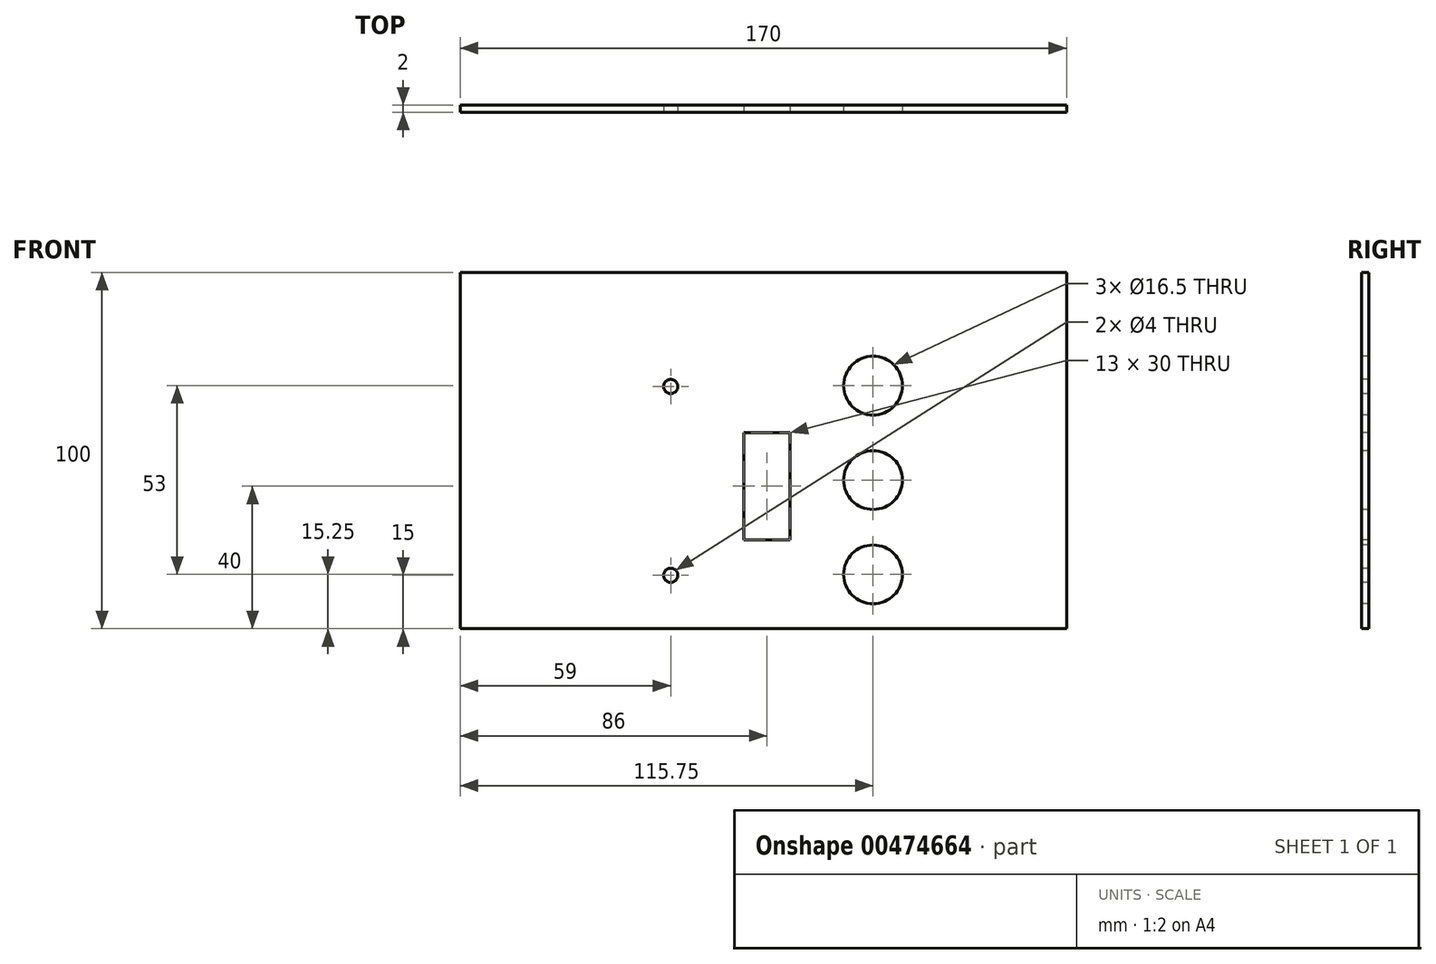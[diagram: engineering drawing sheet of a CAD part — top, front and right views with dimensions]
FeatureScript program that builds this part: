
annotation { "Feature Type Name" : "Feature", "Feature Type Description" : "" }
export const myFeature = defineFeature(function(context is Context, id is Id, definition is map)
    precondition{}
    {
        {
            var Q0;
            Q0=qCreatedBy(makeId("Front.planeOp"),FACE);
            var sketch = newSketch(context, id + "F0", { "sketchPlane" : qUnion([Q0])});
            skLineSegment(sketch, "E0.bottom", {"start": v(85, 50) * mm, "end": v(-85, 50) * mm});
            skLineSegment(sketch, "E0.top", {"start": v(85, -50) * mm, "end": v(-85, -50) * mm});
            skLineSegment(sketch, "E0.left", {"start": v(85, 50) * mm, "end": v(85, -50) * mm});
            skLineSegment(sketch, "E0.right", {"start": v(-85, 50) * mm, "end": v(-85, -50) * mm});
            skPoint(sketch, "E0.middle", {"position": v(0, 0) * mm});
            skSolve(sketch);
        }
        {
            var Q0;
            Q0 = qSketchRegion(id + "F0", true);
            extrude(context, id + "F1", {"entities" : qUnion([Q0]), "depth" : 2 * mm});
        }
        {
            var Q0;
            Q0=makeQuery(id+"F1.opExtrude","CAP_FACE",FACE,{"disambiguationData":[OSD([sQuery(id+"F0.wireOp",EDGE,"E0.bottom"),sQuery(id+"F0.wireOp",EDGE,"E0.top"),sQuery(id+"F0.wireOp",EDGE,"E0.left"),sQuery(id+"F0.wireOp",EDGE,"E0.right")])],"isStart":false});
            var sketch = newSketch(context, id + "F2", { "sketchPlane" : qUnion([Q0])});
            skCircle(sketch, "E1", {"center": v(30.75, -34.75) * mm, "radius": 8.25 * mm});
            skCircle(sketch, "E2", {"center": v(30.75, -8.25) * mm, "radius": 8.25 * mm});
            skCircle(sketch, "E3", {"center": v(30.75, 18.25) * mm, "radius": 8.25 * mm});
            skLineSegment(sketch, "E4.bottom", {"start": v(7.5, -25) * mm, "end": v(-5.5, -25) * mm});
            skLineSegment(sketch, "E4.top", {"start": v(7.5, 5) * mm, "end": v(-5.5, 5) * mm});
            skLineSegment(sketch, "E4.left", {"start": v(7.5, -25) * mm, "end": v(7.5, 5) * mm});
            skLineSegment(sketch, "E4.right", {"start": v(-5.5, -25) * mm, "end": v(-5.5, 5) * mm});
            skPoint(sketch, "E4.middle", {"position": v(1, -10) * mm});
            skCircle(sketch, "E5", {"center": v(-26, -35) * mm, "radius": 2 * mm});
            skCircle(sketch, "E6", {"center": v(-26, 18) * mm, "radius": 2 * mm});
            skSolve(sketch);
        }
        {
            var Q0;
            Q0 = qSketchRegion(id + "F2", true);
            extrude(context, id + "F3", {"entities" : qUnion([Q0]), "operationType" : NewBodyOperationType.REMOVE, "oppositeDirection" : true, "depth" : 25 * mm});
        }
    });
